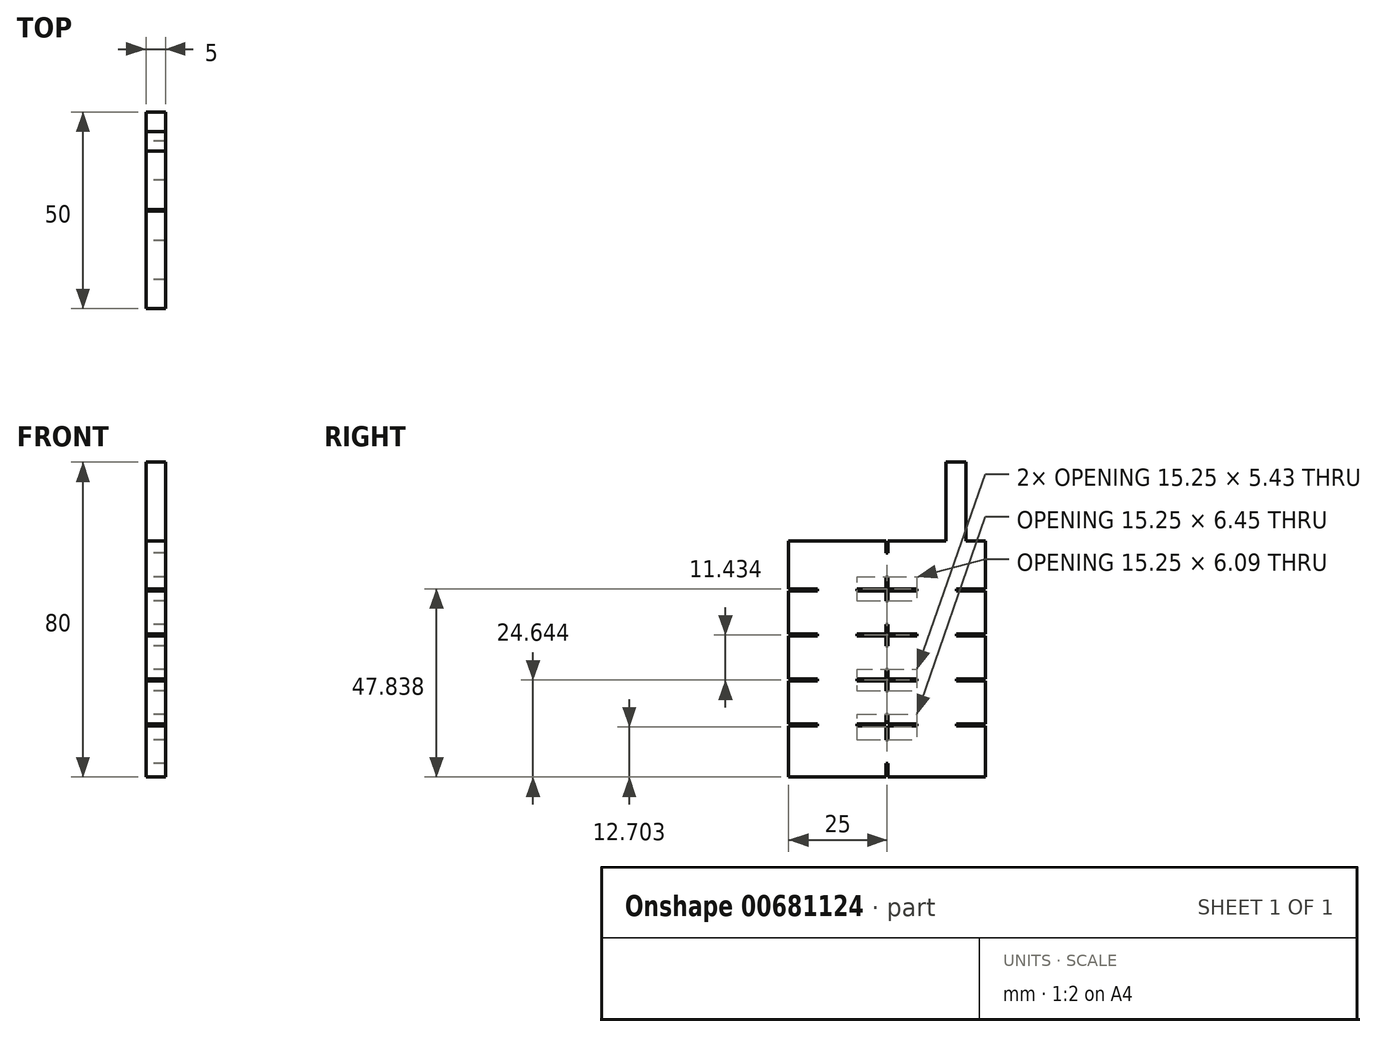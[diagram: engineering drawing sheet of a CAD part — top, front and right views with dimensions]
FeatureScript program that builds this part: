
annotation { "Feature Type Name" : "Feature", "Feature Type Description" : "" }
export const myFeature = defineFeature(function(context is Context, id is Id, definition is map)
    precondition{}
    {
        {
            var Q0;
            Q0=qCreatedBy(makeId("Right.planeOp"),FACE);
            var sketch = newSketch(context, id + "F0", { "sketchPlane" : qUnion([Q0])});
            skPoint(sketch, "E0.0", {"position": v(0, 0) * mm});
            skLineSegment(sketch, "E1.bottom", {"start": v(0, 0) * mm, "end": v(12.38, 0) * mm});
            skLineSegment(sketch, "E1.top", {"start": v(0, -60) * mm, "end": v(24.75, -60) * mm});
            skLineSegment(sketch, "E1.left", {"start": v(0, 0) * mm, "end": v(0, -12.24) * mm});
            skLineSegment(sketch, "E1.right", {"start": v(50, 0) * mm, "end": v(50, -12.24) * mm});
            skPoint(sketch, "E2.MirrorP", {"position": v(11.5, 0) * mm});
            skPoint(sketch, "E3.MirrorP", {"position": v(11.5, -2) * mm});
            skPoint(sketch, "E4.MirrorP", {"position": v(18.5, 0) * mm});
            skPoint(sketch, "E5.MirrorP", {"position": v(30, 0) * mm});
            skLineSegment(sketch, "E6.0", {"start": v(25.25, -60) * mm, "end": v(25.25, -56.52) * mm});
            skLineSegment(sketch, "E7.0", {"start": v(0, -12.24) * mm, "end": v(7.38, -12.24) * mm});
            skLineSegment(sketch, "E8.0", {"start": v(0, -12.74) * mm, "end": v(7.38, -12.74) * mm});
            skLineSegment(sketch, "E9.trimOffspring", {"start": v(25.25, -3.12) * mm, "end": v(25.25, -1.3) * mm});
            skLineSegment(sketch, "E10.trimOffspring", {"start": v(25.25, -12.24) * mm, "end": v(32.63, -12.24) * mm});
            skLineSegment(sketch, "E11.trimOffspring", {"start": v(25.25, -12.24) * mm, "end": v(25.25, -9.12) * mm});
            skLineSegment(sketch, "E12.trimOffspring", {"start": v(25.25, -12.74) * mm, "end": v(32.63, -12.74) * mm});
            skLineSegment(sketch, "E13.trimOffspring", {"start": v(25.25, -15.2) * mm, "end": v(25.25, -12.74) * mm});
            skLineSegment(sketch, "E14.0", {"start": v(0, -23.67) * mm, "end": v(7.38, -23.67) * mm});
            skLineSegment(sketch, "E15.0", {"start": v(0, -24.17) * mm, "end": v(7.38, -24.17) * mm});
            skLineSegment(sketch, "E16.trimOffspring", {"start": v(25.25, -23.67) * mm, "end": v(32.63, -23.67) * mm});
            skLineSegment(sketch, "E17.trimOffspring", {"start": v(25.25, -23.67) * mm, "end": v(25.25, -21.2) * mm});
            skLineSegment(sketch, "E18.trimOffspring", {"start": v(25.25, -24.17) * mm, "end": v(32.63, -24.17) * mm});
            skLineSegment(sketch, "E19.trimOffspring", {"start": v(25.25, -26.64) * mm, "end": v(25.25, -24.17) * mm});
            skLineSegment(sketch, "E20.trimOffspring", {"start": v(24.75, -26.64) * mm, "end": v(24.75, -24.17) * mm});
            skLineSegment(sketch, "E21.0", {"start": v(0, -35.1) * mm, "end": v(7.38, -35.1) * mm});
            skLineSegment(sketch, "E22.0", {"start": v(0, -35.6) * mm, "end": v(7.38, -35.6) * mm});
            skLineSegment(sketch, "E23.trimOffspring", {"start": v(25.25, -35.1) * mm, "end": v(32.63, -35.1) * mm});
            skLineSegment(sketch, "E24.trimOffspring", {"start": v(25.25, -35.1) * mm, "end": v(25.25, -32.64) * mm});
            skLineSegment(sketch, "E25.trimOffspring", {"start": v(24.75, -35.1) * mm, "end": v(24.75, -32.64) * mm});
            skLineSegment(sketch, "E26.trimOffspring", {"start": v(25.25, -35.6) * mm, "end": v(32.63, -35.6) * mm});
            skLineSegment(sketch, "E27.trimOffspring", {"start": v(25.25, -38.07) * mm, "end": v(25.25, -35.6) * mm});
            skLineSegment(sketch, "E28.trimOffspring", {"start": v(24.75, -38.07) * mm, "end": v(24.75, -35.6) * mm});
            skLineSegment(sketch, "E29.0", {"start": v(0, -46.54) * mm, "end": v(7.38, -46.54) * mm});
            skLineSegment(sketch, "E30.0", {"start": v(0, -47.04) * mm, "end": v(7.38, -47.04) * mm});
            skLineSegment(sketch, "E31.trimOffspring", {"start": v(25.25, -46.54) * mm, "end": v(32.63, -46.54) * mm});
            skLineSegment(sketch, "E32.trimOffspring", {"start": v(25.25, -46.54) * mm, "end": v(25.25, -44.07) * mm});
            skLineSegment(sketch, "E33.trimOffspring", {"start": v(24.75, -46.54) * mm, "end": v(24.75, -44.07) * mm});
            skLineSegment(sketch, "E34.trimOffspring", {"start": v(25.25, -47.04) * mm, "end": v(32.63, -47.04) * mm});
            skLineSegment(sketch, "E35.trimOffspring", {"start": v(25.25, -50.52) * mm, "end": v(25.25, -47.04) * mm});
            skLineSegment(sketch, "E36.trimOffspring", {"start": v(0, -12.74) * mm, "end": v(0, -23.67) * mm});
            skLineSegment(sketch, "E37.trimOffspring", {"start": v(0, -24.17) * mm, "end": v(0, -35.1) * mm});
            skLineSegment(sketch, "E38.trimOffspring", {"start": v(0, -35.6) * mm, "end": v(0, -46.54) * mm});
            skLineSegment(sketch, "E39.trimOffspring", {"start": v(0, -47.04) * mm, "end": v(0, -60) * mm});
            skLineSegment(sketch, "E40.trimOffspring", {"start": v(50, -47.04) * mm, "end": v(50, -60) * mm});
            skLineSegment(sketch, "E41.trimOffspring", {"start": v(50, -35.6) * mm, "end": v(50, -46.54) * mm});
            skLineSegment(sketch, "E42.trimOffspring", {"start": v(50, -12.74) * mm, "end": v(50, -23.67) * mm});
            skLineSegment(sketch, "E43.trimOffspring", {"start": v(50, -24.17) * mm, "end": v(50, -35.1) * mm});
            skLineSegment(sketch, "E44.0", {"start": v(17.38, -12.74) * mm, "end": v(17.38, -12.24) * mm});
            skLineSegment(sketch, "E45.0", {"start": v(7.38, -12.74) * mm, "end": v(7.38, -12.24) * mm});
            skLineSegment(sketch, "E46", {"start": v(24.75, -12.24) * mm, "end": v(24.75, -9.12) * mm});
            skLineSegment(sketch, "E47.0", {"start": v(24.75, -9.12) * mm, "end": v(25.25, -9.12) * mm});
            skLineSegment(sketch, "E48.0", {"start": v(24.75, -3.12) * mm, "end": v(25.25, -3.12) * mm});
            skLineSegment(sketch, "E49", {"start": v(24.75, -12.74) * mm, "end": v(24.75, -15.2) * mm});
            skLineSegment(sketch, "E50.0", {"start": v(24.75, -21.2) * mm, "end": v(25.25, -21.2) * mm});
            skLineSegment(sketch, "E51.0", {"start": v(24.75, -15.2) * mm, "end": v(25.25, -15.2) * mm});
            skLineSegment(sketch, "E52", {"start": v(25.25, -1.3) * mm, "end": v(25.25, 0) * mm});
            skLineSegment(sketch, "E53.trimOffspring", {"start": v(25.25, 0) * mm, "end": v(35.12, 0) * mm});
            skPoint(sketch, "E54.start.orphan", {"position": v(24.75, -6.12) * mm});
            skLineSegment(sketch, "E55", {"start": v(7.38, -12.24) * mm, "end": v(7.38, -12.74) * mm});
            skLineSegment(sketch, "E56", {"start": v(17.38, -12.24) * mm, "end": v(17.38, -12.74) * mm});
            skLineSegment(sketch, "E57.trimOffspring", {"start": v(7.38, -23.67) * mm, "end": v(7.38, -24.17) * mm});
            skLineSegment(sketch, "E58.trimOffspring", {"start": v(17.38, -23.67) * mm, "end": v(17.38, -24.17) * mm});
            skLineSegment(sketch, "E59.trimOffspring", {"start": v(7.38, -35.1) * mm, "end": v(7.38, -35.6) * mm});
            skLineSegment(sketch, "E60.trimOffspring", {"start": v(17.38, -35.1) * mm, "end": v(17.38, -35.6) * mm});
            skLineSegment(sketch, "E61.trimOffspring", {"start": v(7.38, -46.54) * mm, "end": v(7.38, -47.04) * mm});
            skLineSegment(sketch, "E62.trimOffspring", {"start": v(17.38, -46.54) * mm, "end": v(17.38, -47.04) * mm});
            skLineSegment(sketch, "E63.trimOffspring", {"start": v(17.38, -46.54) * mm, "end": v(24.75, -46.54) * mm});
            skLineSegment(sketch, "E64.trimOffspring", {"start": v(17.38, -47.04) * mm, "end": v(24.75, -47.04) * mm});
            skLineSegment(sketch, "E65.trimOffspring", {"start": v(17.38, -35.1) * mm, "end": v(24.75, -35.1) * mm});
            skLineSegment(sketch, "E66.trimOffspring", {"start": v(17.38, -35.6) * mm, "end": v(24.75, -35.6) * mm});
            skLineSegment(sketch, "E67.trimOffspring", {"start": v(17.37, -23.67) * mm, "end": v(24.75, -23.67) * mm});
            skLineSegment(sketch, "E68.trimOffspring", {"start": v(17.37, -24.17) * mm, "end": v(24.75, -24.17) * mm});
            skLineSegment(sketch, "E69.trimOffspring", {"start": v(17.38, -12.24) * mm, "end": v(24.75, -12.24) * mm});
            skPoint(sketch, "E70.start.orphan", {"position": v(12.38, -12.74) * mm});
            skPoint(sketch, "E71.orphan", {"position": v(12.38, -12.24) * mm});
            skLineSegment(sketch, "E72.trimOffspring", {"start": v(17.38, -12.74) * mm, "end": v(24.75, -12.74) * mm});
            skLineSegment(sketch, "E73.0", {"start": v(32.63, -12.24) * mm, "end": v(32.63, -12.74) * mm});
            skLineSegment(sketch, "E74.0", {"start": v(42.62, -12.24) * mm, "end": v(42.62, -12.74) * mm});
            skLineSegment(sketch, "E75.trimOffspring", {"start": v(32.63, -23.67) * mm, "end": v(32.63, -24.17) * mm});
            skLineSegment(sketch, "E76.trimOffspring", {"start": v(42.62, -23.67) * mm, "end": v(42.62, -24.17) * mm});
            skLineSegment(sketch, "E77.trimOffspring", {"start": v(32.63, -35.1) * mm, "end": v(32.63, -35.6) * mm});
            skLineSegment(sketch, "E78.trimOffspring", {"start": v(42.62, -35.1) * mm, "end": v(42.62, -35.6) * mm});
            skLineSegment(sketch, "E79.trimOffspring", {"start": v(32.63, -46.54) * mm, "end": v(32.63, -47.04) * mm});
            skLineSegment(sketch, "E80.trimOffspring", {"start": v(42.62, -46.54) * mm, "end": v(42.62, -47.04) * mm});
            skLineSegment(sketch, "E81.0", {"start": v(24.75, -26.64) * mm, "end": v(25.25, -26.64) * mm});
            skLineSegment(sketch, "E82.0", {"start": v(24.75, -32.64) * mm, "end": v(25.25, -32.64) * mm});
            skLineSegment(sketch, "E83.0", {"start": v(24.75, -38.07) * mm, "end": v(25.25, -38.07) * mm});
            skLineSegment(sketch, "E84.0", {"start": v(24.75, -44.07) * mm, "end": v(25.25, -44.07) * mm});
            skLineSegment(sketch, "E85", {"start": v(24.75, -47.04) * mm, "end": v(24.75, -50.52) * mm});
            skLineSegment(sketch, "E86.0", {"start": v(24.75, -56.52) * mm, "end": v(25.25, -56.52) * mm});
            skLineSegment(sketch, "E87.0", {"start": v(24.75, -50.52) * mm, "end": v(25.25, -50.52) * mm});
            skLineSegment(sketch, "E88.trimOffspring", {"start": v(24.75, -56.52) * mm, "end": v(24.75, -60) * mm});
            skLineSegment(sketch, "E89.trimOffspring", {"start": v(25.25, -60) * mm, "end": v(50, -60) * mm});
            skLineSegment(sketch, "E90.trimOffspring", {"start": v(42.62, -46.54) * mm, "end": v(50, -46.54) * mm});
            skLineSegment(sketch, "E91.trimOffspring", {"start": v(42.62, -47.04) * mm, "end": v(50, -47.04) * mm});
            skLineSegment(sketch, "E92.trimOffspring", {"start": v(42.62, -35.1) * mm, "end": v(50, -35.1) * mm});
            skLineSegment(sketch, "E93.trimOffspring", {"start": v(42.62, -35.6) * mm, "end": v(50, -35.6) * mm});
            skLineSegment(sketch, "E94.trimOffspring", {"start": v(42.62, -23.67) * mm, "end": v(50, -23.67) * mm});
            skLineSegment(sketch, "E95.trimOffspring", {"start": v(42.62, -24.17) * mm, "end": v(50, -24.17) * mm});
            skLineSegment(sketch, "E96.trimOffspring", {"start": v(42.62, -12.24) * mm, "end": v(50, -12.24) * mm});
            skLineSegment(sketch, "E97.trimOffspring", {"start": v(42.62, -12.74) * mm, "end": v(50, -12.74) * mm});
            skLineSegment(sketch, "E98.trimOffspring", {"start": v(24.75, -21.2) * mm, "end": v(24.75, -23.67) * mm});
            skPoint(sketch, "E99.end.orphan", {"position": v(25.25, -18.2) * mm});
            skPoint(sketch, "E99.start.orphan", {"position": v(24.75, -18.2) * mm});
            skPoint(sketch, "E100.orphan", {"position": v(25.25, -17.95) * mm});
            skPoint(sketch, "E101.end.orphan", {"position": v(25.25, -18.45) * mm});
            skLineSegment(sketch, "E102.trimOffspring", {"start": v(24.75, -3.12) * mm, "end": v(24.75, 0) * mm});
            skPoint(sketch, "E103.orphan", {"position": v(14.88, 25) * mm});
            skPoint(sketch, "E104.orphan", {"position": v(37.63, 25) * mm});
            skLineSegment(sketch, "E105.trimOffspring", {"start": v(14.88, 0) * mm, "end": v(24.75, 0) * mm});
            skLineSegment(sketch, "E106.trimOffspring", {"start": v(37.63, 0) * mm, "end": v(40, 0) * mm});
            skLineSegment(sketch, "E107", {"start": v(35.12, 0) * mm, "end": v(40, 0) * mm});
            skLineSegment(sketch, "E108.0", {"start": v(45, 0) * mm, "end": v(45, 15) * mm});
            skLineSegment(sketch, "E109.0", {"start": v(40, 0) * mm, "end": v(40, 15) * mm});
            skLineSegment(sketch, "E110", {"start": v(14.88, 0) * mm, "end": v(11.5, 0) * mm});
            skLineSegment(sketch, "E111.trimOffspring", {"start": v(45, 0) * mm, "end": v(50, 0) * mm});
            skLineSegment(sketch, "E112.0", {"start": v(40, 20) * mm, "end": v(45, 20) * mm});
            skLineSegment(sketch, "E113", {"start": v(40, 20) * mm, "end": v(40, 15) * mm});
            skLineSegment(sketch, "E114", {"start": v(45, 20) * mm, "end": v(45, 15) * mm});
            skSolve(sketch);
        }
        {
            var Q0;
            {var subQ1=sQuery(id+"F0.wireOp",EDGE,"6f222dcf-cafe-427f-96f1-de862232ba62.0");Q0=makeQuery(id+"F0.imprint","IMPRINT",FACE,{"disambiguationData":[TD([[makeQuery(id+"F0.imprint","IMPRINT",EDGE,{"derivedFrom":subQ1}),-1.0]])]});}
            var Q1;
            {var subQ1=sQuery(id+"F0.wireOp",EDGE,"9ddca581-0f96-48d2-9b8e-d0e5be099db1.trimOffspring");Q1=makeQuery(id+"F0.imprint","IMPRINT",FACE,{"disambiguationData":[TD([[makeQuery(id+"F0.imprint","IMPRINT",EDGE,{"derivedFrom":subQ1}),-1.0]])]});}
            var Q2;
            Q2=makeQuery(id+"F0.imprint","IMPRINT",FACE,{"disambiguationData":[TD([[makeQuery(id+"F0.imprint","IMPRINT",EDGE,{"derivedFrom":sQuery(id+"F0.wireOp",EDGE,"E8.0")}),-1.0]])]});
            var Q3;
            Q3=makeQuery(id+"F0.imprint","IMPRINT",FACE,{"disambiguationData":[TD([[makeQuery(id+"F0.imprint","IMPRINT",EDGE,{"derivedFrom":sQuery(id+"F0.wireOp",EDGE,"E12.trimOffspring")}),-1.0]])]});
            var Q4;
            Q4=makeQuery(id+"F0.imprint","IMPRINT",FACE,{"disambiguationData":[TD([[makeQuery(id+"F0.imprint","IMPRINT",EDGE,{"derivedFrom":sQuery(id+"F0.wireOp",EDGE,"E18.trimOffspring")}),-1.0]])]});
            var Q5;
            Q5=makeQuery(id+"F0.imprint","IMPRINT",FACE,{"disambiguationData":[TD([[makeQuery(id+"F0.imprint","IMPRINT",EDGE,{"derivedFrom":sQuery(id+"F0.wireOp",EDGE,"E15.0")}),-1.0]])]});
            var Q6;
            Q6=makeQuery(id+"F0.imprint","IMPRINT",FACE,{"disambiguationData":[TD([[makeQuery(id+"F0.imprint","IMPRINT",EDGE,{"derivedFrom":sQuery(id+"F0.wireOp",EDGE,"E22.0")}),-1.0]])]});
            var Q7;
            Q7=makeQuery(id+"F0.imprint","IMPRINT",FACE,{"disambiguationData":[TD([[makeQuery(id+"F0.imprint","IMPRINT",EDGE,{"derivedFrom":sQuery(id+"F0.wireOp",EDGE,"E26.trimOffspring")}),-1.0]])]});
            var Q8;
            {var subQ0=sQuery(id+"F0.wireOp",EDGE,"E6.0");Q8=makeQuery(id+"F0.imprint","IMPRINT",FACE,{"disambiguationData":[TD([[makeQuery(id+"F0.imprint","IMPRINT",EDGE,{"derivedFrom":subQ0}),-1.0]])]});}
            var Q9;
            {var subQ0=sQuery(id+"F0.wireOp",EDGE,"52d86100-12cc-4532-affd-39e9c9b04a49.0");Q9=makeQuery(id+"F0.imprint","IMPRINT",FACE,{"disambiguationData":[TD([[makeQuery(id+"F0.imprint","IMPRINT",EDGE,{"derivedFrom":subQ0}),1.0]])]});}
            extrude(context, id + "F1", {"entities" : qUnion([Q0, Q1, Q2, Q3, Q4, Q5, Q6, Q7, Q8, Q9]), "depth" : 5 * mm, "offsetDistance" : 25 * mm});
        }
    });
